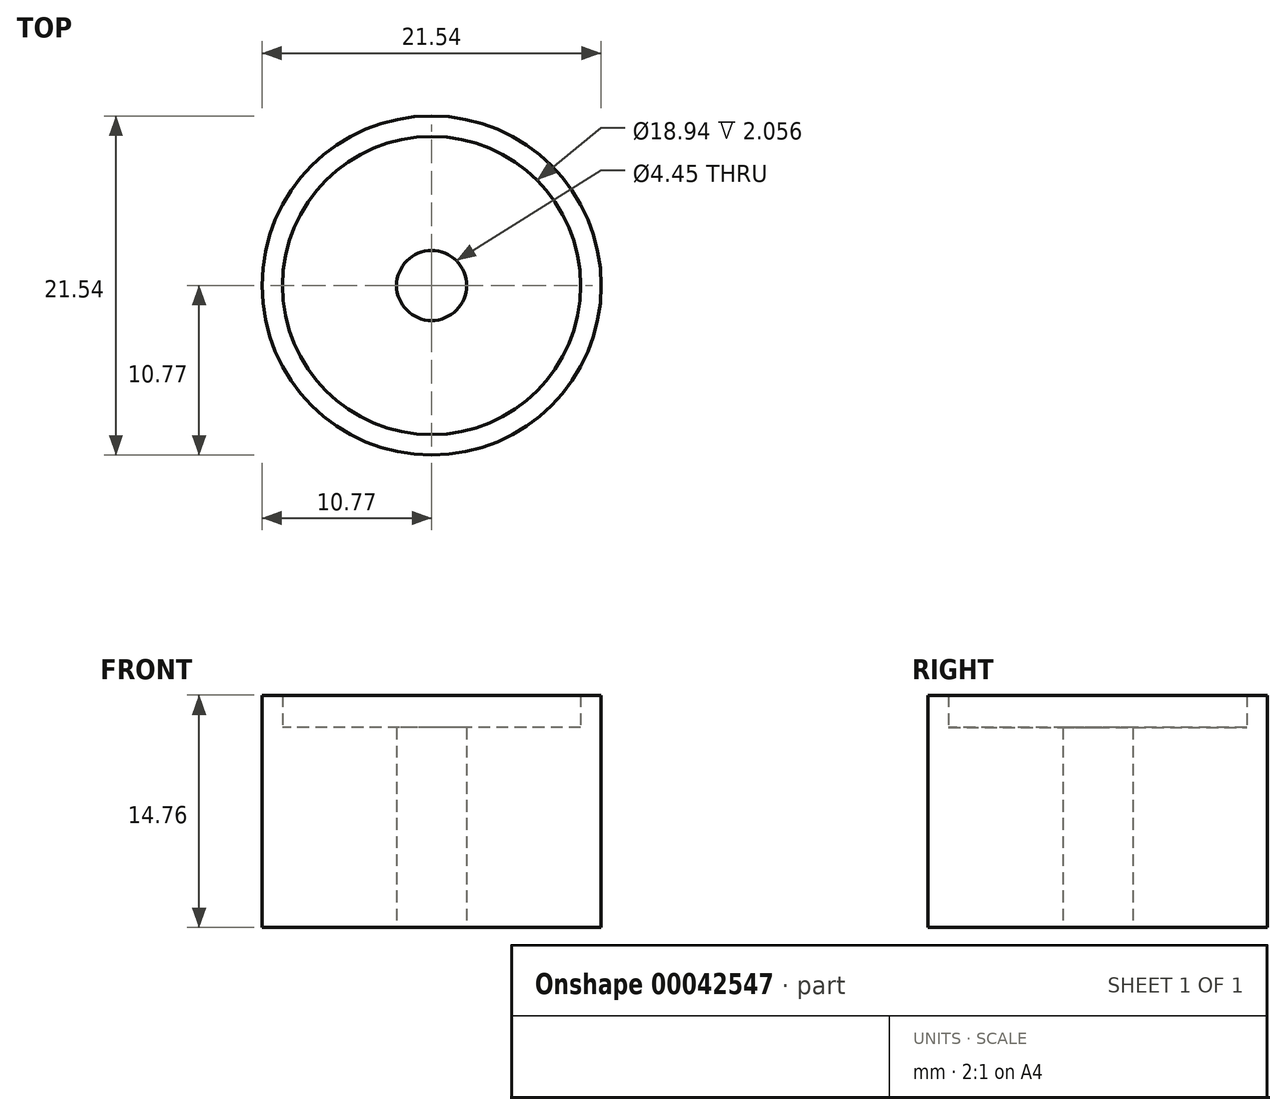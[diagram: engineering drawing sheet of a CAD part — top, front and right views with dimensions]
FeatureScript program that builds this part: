
annotation { "Feature Type Name" : "Feature", "Feature Type Description" : "" }
export const myFeature = defineFeature(function(context is Context, id is Id, definition is map)
    precondition{}
    {
        {
            var Q0;
            Q0=qCreatedBy(makeId("Top.planeOp"),FACE);
            var sketch = newSketch(context, id + "F0", { "sketchPlane" : qUnion([Q0])});
            skCircle(sketch, "E0", {"center": v(0, 0) * mm, "radius": 10.77 * mm});
            skCircle(sketch, "E1", {"center": v(0, 0) * mm, "radius": 9.47 * mm});
            skCircle(sketch, "E2", {"center": v(0, 0) * mm, "radius": 3.3 * mm});
            skSolve(sketch);
        }
        {
            var Q0;
            Q0=makeQuery(id+"F0.imprint","IMPRINT",FACE,{"disambiguationData":[TD([[makeQuery(id+"F0.imprint","IMPRINT",EDGE,{"derivedFrom":sQuery(id+"F0.wireOp",EDGE,"E0")}),1.0]])]});
            extrude(context, id + "F1", {"entities" : qUnion([Q0]), "depth" : 14.76 * mm});
        }
        {
            var Q0;
            Q0=qCreatedBy(makeId("Top.planeOp"),FACE);
            var sketch = newSketch(context, id + "F2", { "sketchPlane" : qUnion([Q0])});
            skCircle(sketch, "E3", {"center": v(0, 0) * mm, "radius": 9.57 * mm});
            skCircle(sketch, "E4", {"center": v(0, 0) * mm, "radius": 2.22 * mm});
            skSolve(sketch);
        }
        {
            var Q0;
            Q0=makeQuery(id+"F2.imprint","IMPRINT",FACE,{"disambiguationData":[TD([[makeQuery(id+"F2.imprint","IMPRINT",EDGE,{"derivedFrom":sQuery(id+"F2.wireOp",EDGE,"E3")}),1.0]])]});
            extrude(context, id + "F3", {"entities" : qUnion([Q0]), "operationType" : NewBodyOperationType.ADD, "depth" : 12.7 * mm});
        }
    });
